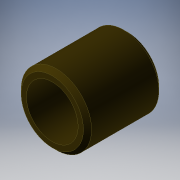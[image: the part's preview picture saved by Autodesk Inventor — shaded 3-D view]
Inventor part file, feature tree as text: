
AUTODESK INVENTOR PART (.ipt)
format: ipt  version: 2019 (Build 230136000, 136)  size: 133,632 bytes
history: native  units: in
note: dims shown in document units (in); Inventor stores cm internally (conversion verified against a paired STEP export)
features: other x35, revolve x1, sketch x1
ambient origin geometry x8: Origin, YZ Plane, XZ Plane, XY Plane, X Axis, Y Axis, Z Axis, Center Point
bodies: Solid1 (feature_tree)
feature tree (37):
  revolve  "Revolution1"  [1 undecoded]
  other  "bushing_XY"
  other  "bushing_YZ"
  other  "bushing_ZX"
  other  "bushing_X"
  other  "bushing_Y"
  other  "bushing_Z"
  other  "bushing_Center"
  other  "id1_XY"
  other  "id1_YZ"
  other  "id1_ZX"
  other  "id1_X"
  other  "id1_Y"
  other  "id1_Z"
  other  "id1_Center"
  other  "id2_XY"
  other  "id2_YZ"
  other  "id2_ZX"
  other  "id2_X"
  other  "id2_Y"
  other  "id2_Z"
  other  "id2_Center"
  other  "id3_XY"
  other  "id3_YZ"
  other  "id3_ZX"
  other  "id3_X"
  other  "id3_Y"
  other  "id3_Z"
  other  "id3_Center"
  other  "id4_XY"
  other  "id4_YZ"
  other  "id4_ZX"
  other  "id4_X"
  other  "id4_Y"
  other  "id4_Z"
  other  "id4_Center"
  sketch  "Sketch_1"  dims[d0=360.0deg d1=0.0in d2=0.0in]
note: 1 required parameter value undecoded (feature->parameter linkage not recoverable at this tier; creation-order binding heuristic only, values carry confidence <= 0.55)
